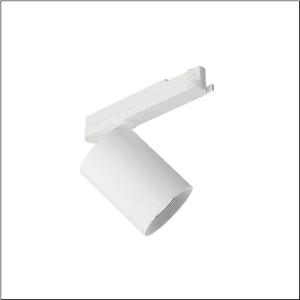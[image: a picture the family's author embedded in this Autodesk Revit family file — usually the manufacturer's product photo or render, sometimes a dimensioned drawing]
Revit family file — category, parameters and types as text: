
# Revit family: spot_21_51se12mba5b
name_source: partatom
category: Lighting Fixtures
units: mm (PartAtom-declared; Revit-internal decimal feet)

## family parameters
Cut with Voids When Loaded = No
Host = Face
Light Source = No
Part Type = Normal
Room Calculation Point = No
Round Connector Dimension = Use Diameter
Shared = No

## types (1)
- --- (1 x LED, 5240 lm, 41.7 W, 2700K)
    Apparent Load = 42 VA
    CIE Flux Codes = 95 98 99 100 100
    Color Rendering = 90
    Color Temperature = 2700K
    Default Elevation = 1800 mm
    Description = Spot 21, directional spotlight, light control with lens, of PMMA, LED rated luminous flux: 5.040lm, light colour: 927, control gear: ECG Multilumen, with 3-phase adapter, mains connection: 220..240V, AC, 50/60Hz, of aluminium, traffic white (RAL 9016), length: 213mm, diameter: 105mm, protection rating (complete): IP20, insulation class (complete): insulation class I (protective earthing), certification: CE, impact resistance: IK02, permissible ambient temperature for indoor applications: -20..+40°C, packaging unit: 1 piece
    Height = 175 mm
    Lamp = 1 x LED
    Lamp Light Flux = 5240 lm
    Lamp Power = 41.7 W
    Lamp count = 1
    Length = 105 mm
    Luminous efficacy = 126 lm/W
    Manufacturer = Siteco
    ModVariant = No
    Model = 51SE12MBA5B
    Mounting Place = Ceiling
    Mounting Type = Pendant
    Number of Poles = 1
    OnlyDefault = Yes
    Power Factor = 1
    Product Name = Spot 21
    Product group = directional spotlight
    ProductGroupID = 905
    Protection Class = Protection class I
    Protection Degree = IP 20
    RLX_Detail_Level = 1
    RLX_Emergency_Light_Flux = 0 lm
    RLX_Emergency_Type = 0
    RLX_Emergency_Type_DB = No
    RlxData = <blob elided: 17637 chars, md5=f0c2de4d>
    Socket = socket
    Standby Power = 0 W
    System Light Flux = 5240 lm
    System Power = 42 W
    Type Comments = factory setting: luminous flux: 100 % | (ON | ON | ON | ON) | 1050 mA
    Type Image = l_1003976.jpg
    URL = http://relux.com
    VarID = @adj_114435
    Voltage = 0 V
    Weight = 0.00 kg
    Width = 0 mm  [stored 0 ft]

note: [stored X ft] marks values corroborated as IEEE doubles in the binary element streams (Revit-internal decimal feet)

## geometry (parser evidence)
native form markers: Blend x4, Sweep x11
no freeform markers — native parametric forms only
